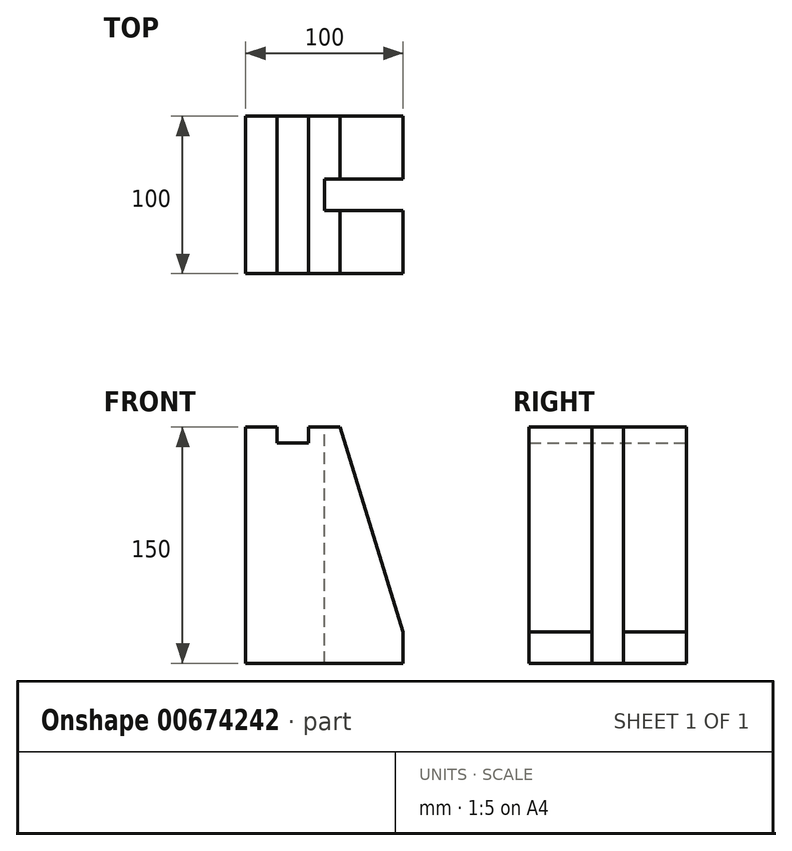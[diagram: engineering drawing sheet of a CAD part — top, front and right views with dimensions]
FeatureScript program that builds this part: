
annotation { "Feature Type Name" : "Feature", "Feature Type Description" : "" }
export const myFeature = defineFeature(function(context is Context, id is Id, definition is map)
    precondition{}
    {
        {
            var Q0;
            Q0=qCreatedBy(makeId("Front.planeOp"),FACE);
            var sketch = newSketch(context, id + "F0", { "sketchPlane" : qUnion([Q0])});
            skLineSegment(sketch, "E0", {"start": v(0, 0) * mm, "end": v(100, 0) * mm});
            skLineSegment(sketch, "E1", {"start": v(100, 0) * mm, "end": v(100, 20) * mm});
            skLineSegment(sketch, "E2", {"start": v(0, 0) * mm, "end": v(0, 150) * mm});
            skLineSegment(sketch, "E3", {"start": v(60, 150) * mm, "end": v(100, 20) * mm});
            skLineSegment(sketch, "E4", {"start": v(0, 150) * mm, "end": v(20, 150) * mm});
            skLineSegment(sketch, "E5", {"start": v(20, 150) * mm, "end": v(20, 140) * mm});
            skLineSegment(sketch, "E6", {"start": v(20, 140) * mm, "end": v(40, 140) * mm});
            skLineSegment(sketch, "E7", {"start": v(40, 140) * mm, "end": v(40, 150) * mm});
            skLineSegment(sketch, "E8", {"start": v(40, 150) * mm, "end": v(60, 150) * mm});
            skSolve(sketch);
        }
        {
            var Q0;
            Q0=makeQuery(id+"F0.imprint","IMPRINT",FACE,{"disambiguationData":[TD([[makeQuery(id+"F0.imprint","IMPRINT",EDGE,{"derivedFrom":sQuery(id+"F0.wireOp",EDGE,"E0")}),1.0]])]});
            extrude(context, id + "F1", {"entities" : qUnion([Q0]), "depth" : 100 * mm, "offsetDistance" : 25 * mm});
        }
        {
            var Q0;
            Q0=makeQuery(id+"F1.opExtrude","SWEPT_FACE",FACE,{"disambiguationData":[OSD([sQuery(id+"F0.wireOp",EDGE,"E8")])]});
            var sketch = newSketch(context, id + "F2", { "sketchPlane" : qUnion([Q0])});
            skLineSegment(sketch, "E9", {"start": v(60, -60) * mm, "end": v(50, -60) * mm});
            skLineSegment(sketch, "E10", {"start": v(50, -60) * mm, "end": v(50, -40) * mm});
            skLineSegment(sketch, "E11", {"start": v(50, -40) * mm, "end": v(60, -40) * mm});
            skLineSegment(sketch, "E12.bottom", {"start": v(50, -40) * mm, "end": v(101, -40) * mm});
            skLineSegment(sketch, "E12.top", {"start": v(50, -60) * mm, "end": v(101, -60) * mm});
            skLineSegment(sketch, "E12.right", {"start": v(101, -40) * mm, "end": v(101, -60) * mm});
            skSolve(sketch);
        }
        {
            var Q0;
            {var subQ0=sQuery(id+"F2.wireOp",EDGE,"E12.right");Q0=makeQuery(id+"F2.imprint","IMPRINT",FACE,{"disambiguationData":[TD([[makeQuery(id+"F2.imprint","IMPRINT",EDGE,{"derivedFrom":subQ0}),-1.0]])]});}
            var Q1;
            {var subQ0=sQuery(id+"F2.wireOp",EDGE,"E10");Q1=makeQuery(id+"F2.imprint","IMPRINT",FACE,{"disambiguationData":[TD([[makeQuery(id+"F2.imprint","IMPRINT",EDGE,{"derivedFrom":subQ0}),-1.0]])]});}
            extrude(context, id + "F3", {"entities" : qUnion([Q0, Q1]), "operationType" : NewBodyOperationType.REMOVE, "oppositeDirection" : true, "depth" : 150 * mm, "offsetDistance" : 25 * mm});
        }
    });
